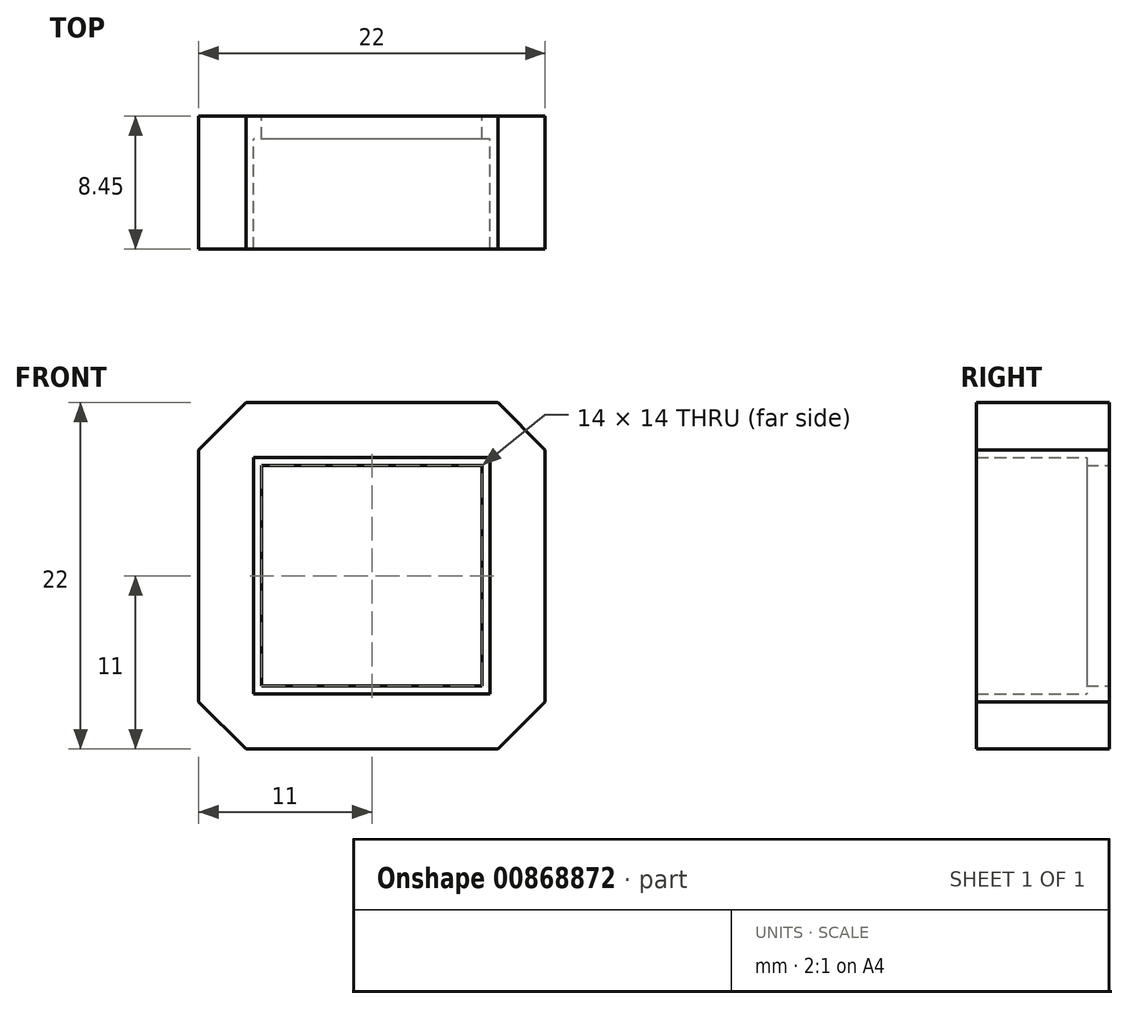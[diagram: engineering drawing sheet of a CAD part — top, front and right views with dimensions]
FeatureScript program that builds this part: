
annotation { "Feature Type Name" : "Feature", "Feature Type Description" : "" }
export const myFeature = defineFeature(function(context is Context, id is Id, definition is map)
    precondition{}
    {
        {
            var Q0;
            Q0=qCreatedBy(makeId("Front.planeOp"),FACE);
            var sketch = newSketch(context, id + "F0", { "sketchPlane" : qUnion([Q0])});
            skLineSegment(sketch, "E0.bottom", {"start": v(7, 7) * mm, "end": v(-7, 7) * mm});
            skLineSegment(sketch, "E0.top", {"start": v(7, -7) * mm, "end": v(-7, -7) * mm});
            skLineSegment(sketch, "E0.left", {"start": v(7, 7) * mm, "end": v(7, -7) * mm});
            skLineSegment(sketch, "E0.right", {"start": v(-7, 7) * mm, "end": v(-7, -7) * mm});
            skPoint(sketch, "E0.middle", {"position": v(0, 0) * mm});
            skLineSegment(sketch, "E1.bottom", {"start": v(11, 11) * mm, "end": v(-11, 11) * mm});
            skLineSegment(sketch, "E1.top", {"start": v(11, -11) * mm, "end": v(-11, -11) * mm});
            skLineSegment(sketch, "E1.left", {"start": v(11, 11) * mm, "end": v(11, -11) * mm});
            skLineSegment(sketch, "E1.right", {"start": v(-11, 11) * mm, "end": v(-11, -11) * mm});
            skSolve(sketch);
        }
        {
            var Q0;
            Q0=makeQuery(id+"F0.imprint","IMPRINT",FACE,{"disambiguationData":[TD([[makeQuery(id+"F0.imprint","IMPRINT",EDGE,{"derivedFrom":sQuery(id+"F0.wireOp",EDGE,"E0.bottom")}),-1.0]])]});
            extrude(context, id + "F1", {"entities" : qUnion([Q0]), "depth" : 1.45 * mm, "offsetDistance" : 25 * mm});
        }
        {
            var Q0;
            Q0=makeQuery(id+"F1.opExtrude","CAP_FACE",FACE,{"disambiguationData":[OSD([sQuery(id+"F0.wireOp",EDGE,"E0.bottom"),sQuery(id+"F0.wireOp",EDGE,"E0.top"),sQuery(id+"F0.wireOp",EDGE,"E0.left"),sQuery(id+"F0.wireOp",EDGE,"E0.right"),sQuery(id+"F0.wireOp",EDGE,"E1.bottom"),sQuery(id+"F0.wireOp",EDGE,"E1.top"),sQuery(id+"F0.wireOp",EDGE,"E1.left"),sQuery(id+"F0.wireOp",EDGE,"E1.right")])],"isStart":false});
            var sketch = newSketch(context, id + "F2", { "sketchPlane" : qUnion([Q0])});
            skLineSegment(sketch, "E2.bottom", {"start": v(7.5, 7.5) * mm, "end": v(-7.5, 7.5) * mm});
            skLineSegment(sketch, "E2.top", {"start": v(7.5, -7.5) * mm, "end": v(-7.5, -7.5) * mm});
            skLineSegment(sketch, "E2.left", {"start": v(7.5, 7.5) * mm, "end": v(7.5, -7.5) * mm});
            skLineSegment(sketch, "E2.right", {"start": v(-7.5, 7.5) * mm, "end": v(-7.5, -7.5) * mm});
            skPoint(sketch, "E2.middle", {"position": v(0, 0) * mm});
            skSolve(sketch);
        }
        {
            var Q0;
            Q0=makeQuery(id+"F2.imprint","IMPRINT",FACE,{"disambiguationData":[TD([[makeQuery(id+"F2.imprint","IMPRINT",EDGE,{"derivedFrom":sQuery(id+"F2.wireOp",EDGE,"E2.bottom")}),-1.0]])]});
            extrude(context, id + "F3", {"entities" : qUnion([Q0]), "operationType" : NewBodyOperationType.ADD, "depth" : 7 * mm, "offsetDistance" : 25 * mm});
        }
        {
            var Q0;
            {var subQ0=sQuery(id+"F0.wireOp",EDGE,"E1.right");var subQ1=sQuery(id+"F0.wireOp",EDGE,"E1.bottom");Q0=makeQuery(id+"F3.boolean.opBoolean","MERGE",EDGE,{"derivedFrom":[makeQuery(id+"F1.opExtrude","SWEPT_EDGE",EDGE,{"disambiguationData":[OSD([subQ1,subQ0])]}),makeQuery(id+"F3.opExtrude","SWEPT_EDGE",EDGE,{"disambiguationData":[OSD([subQ1,subQ0])]})]});}
            var Q1;
            {var subQ0=sQuery(id+"F0.wireOp",EDGE,"E1.left");var subQ1=sQuery(id+"F0.wireOp",EDGE,"E1.bottom");Q1=makeQuery(id+"F3.boolean.opBoolean","MERGE",EDGE,{"derivedFrom":[makeQuery(id+"F1.opExtrude","SWEPT_EDGE",EDGE,{"disambiguationData":[OSD([subQ1,subQ0])]}),makeQuery(id+"F3.opExtrude","SWEPT_EDGE",EDGE,{"disambiguationData":[OSD([subQ1,subQ0])]})]});}
            var Q2;
            {var subQ0=sQuery(id+"F0.wireOp",EDGE,"E1.left");var subQ1=sQuery(id+"F0.wireOp",EDGE,"E1.top");Q2=makeQuery(id+"F3.boolean.opBoolean","MERGE",EDGE,{"derivedFrom":[makeQuery(id+"F1.opExtrude","SWEPT_EDGE",EDGE,{"disambiguationData":[OSD([subQ1,subQ0])]}),makeQuery(id+"F3.opExtrude","SWEPT_EDGE",EDGE,{"disambiguationData":[OSD([subQ1,subQ0])]})]});}
            var Q3;
            {var subQ0=sQuery(id+"F0.wireOp",EDGE,"E1.right");var subQ1=sQuery(id+"F0.wireOp",EDGE,"E1.top");Q3=makeQuery(id+"F3.boolean.opBoolean","MERGE",EDGE,{"derivedFrom":[makeQuery(id+"F1.opExtrude","SWEPT_EDGE",EDGE,{"disambiguationData":[OSD([subQ1,subQ0])]}),makeQuery(id+"F3.opExtrude","SWEPT_EDGE",EDGE,{"disambiguationData":[OSD([subQ1,subQ0])]})]});}
            chamfer(context, id + "F4", {"entities" : qUnion([Q0, Q1, Q2, Q3]), "width" : 3 * mm, "tangentPropagation" : true});
        }
    });
